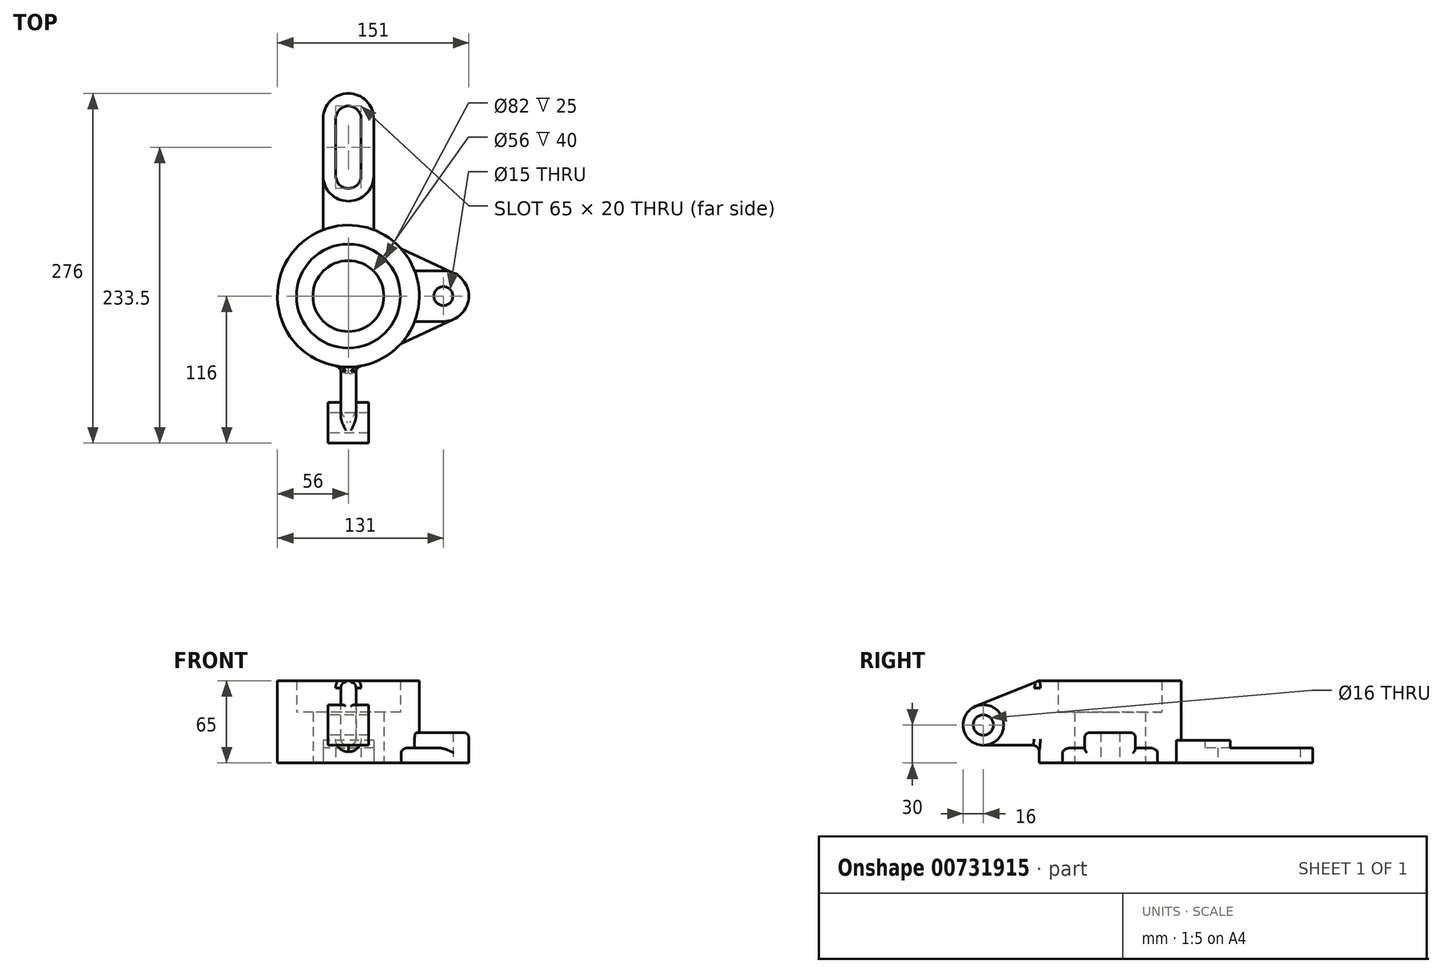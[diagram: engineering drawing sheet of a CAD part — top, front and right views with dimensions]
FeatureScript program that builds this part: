
annotation { "Feature Type Name" : "Feature", "Feature Type Description" : "" }
export const myFeature = defineFeature(function(context is Context, id is Id, definition is map)
    precondition{}
    {
        {
            var Q0;
            Q0=qCreatedBy(makeId("Top.planeOp"),FACE);
            var sketch = newSketch(context, id + "F0", { "sketchPlane" : qUnion([Q0])});
            skCircle(sketch, "E0", {"center": v(0, 0) * mm, "radius": 28 * mm});
            skCircle(sketch, "E1", {"center": v(0, 0) * mm, "radius": 41 * mm});
            skCircle(sketch, "E2", {"center": v(0, 0) * mm, "radius": 56 * mm});
            skSolve(sketch);
        }
        {
            var Q0;
            Q0=makeQuery(id+"F0.imprint","IMPRINT",FACE,{"disambiguationData":[TD([[makeQuery(id+"F0.imprint","IMPRINT",EDGE,{"derivedFrom":sQuery(id+"F0.wireOp",EDGE,"E1")}),-1.0]])]});
            extrude(context, id + "F1", {"entities" : qUnion([Q0]), "depth" : 65 * mm, "offsetDistance" : 25 * mm});
        }
        {
            var Q0;
            Q0=makeQuery(id+"F0.imprint","IMPRINT",FACE,{"disambiguationData":[TD([[makeQuery(id+"F0.imprint","IMPRINT",EDGE,{"derivedFrom":sQuery(id+"F0.wireOp",EDGE,"E0")}),-1.0]])]});
            extrude(context, id + "F2", {"entities" : qUnion([Q0]), "operationType" : NewBodyOperationType.ADD, "depth" : (65 - 25) * mm, "offsetDistance" : 25 * mm});
        }
        {
            var Q0;
            Q0=qCreatedBy(makeId("Top.planeOp"),FACE);
            var sketch = newSketch(context, id + "F3", { "sketchPlane" : qUnion([Q0])});
            skLineSegment(sketch, "E3", {"start": v(0, 95) * mm, "end": v(0, 140) * mm, "construction": true});
            skArc(sketch, "E4.0.startCap", {"start": v(20, 95) * mm, "mid": v(0, 75) * mm, "end": v(-20, 95) * mm});
            skArc(sketch, "E4.0.endCap", {"start": v(-20, 140) * mm, "mid": v(0, 160) * mm, "end": v(20, 140) * mm});
            skLineSegment(sketch, "E4.0.left", {"start": v(-20, 95) * mm, "end": v(-20, 140) * mm});
            skLineSegment(sketch, "E4.0.right", {"start": v(20, 95) * mm, "end": v(20, 140) * mm});
            skArc(sketch, "E5.0.startCap", {"start": v(10, 95) * mm, "mid": v(0, 85) * mm, "end": v(-10, 95) * mm});
            skArc(sketch, "E5.0.endCap", {"start": v(-10, 140) * mm, "mid": v(0, 150) * mm, "end": v(10, 140) * mm});
            skLineSegment(sketch, "E5.0.left", {"start": v(-10, 95) * mm, "end": v(-10, 140) * mm});
            skLineSegment(sketch, "E5.0.right", {"start": v(10, 95) * mm, "end": v(10, 140) * mm});
            skCircle(sketch, "E6.0", {"center": v(0, 0) * mm, "radius": 56 * mm});
            skLineSegment(sketch, "E7", {"start": v(-20, 95) * mm, "end": v(-20, 52.3) * mm});
            skLineSegment(sketch, "E8", {"start": v(20, 95) * mm, "end": v(20, 52.3) * mm});
            skSolve(sketch);
        }
        {
            var Q0;
            Q0=makeQuery(id+"F3.imprint","IMPRINT",FACE,{"disambiguationData":[TD([[makeQuery(id+"F3.imprint","IMPRINT",EDGE,{"derivedFrom":sQuery(id+"F3.wireOp",EDGE,"E4.0.startCap")}),1.0]])]});
            extrude(context, id + "F4", {"entities" : qUnion([Q0]), "operationType" : NewBodyOperationType.ADD, "depth" : 12 * mm, "offsetDistance" : 25 * mm});
        }
        {
            var Q0;
            Q0=makeQuery(id+"F3.imprint","IMPRINT",FACE,{"disambiguationData":[TD([[makeQuery(id+"F3.imprint","IMPRINT",EDGE,{"derivedFrom":sQuery(id+"F3.wireOp",EDGE,"E4.0.startCap")}),-1.0]])]});
            extrude(context, id + "F5", {"entities" : qUnion([Q0]), "operationType" : NewBodyOperationType.ADD, "depth" : 18 * mm, "offsetDistance" : 25 * mm});
        }
        {
            var Q0;
            Q0=qCreatedBy(makeId("Right.planeOp"),FACE);
            var sketch = newSketch(context, id + "F6", { "sketchPlane" : qUnion([Q0])});
            skCircle(sketch, "E9", {"center": v(-100, 30) * mm, "radius": 16 * mm});
            skCircle(sketch, "E10", {"center": v(-100, 30) * mm, "radius": 8 * mm});
            skLineSegment(sketch, "E11.0", {"start": v(-56, 65) * mm, "end": v(56, 65) * mm});
            skLineSegment(sketch, "E12", {"start": v(-56, 0) * mm, "end": v(-56, 65) * mm});
            skLineSegment(sketch, "E13", {"start": v(-56, 65) * mm, "end": v(-105.99, 44.84) * mm});
            skLineSegment(sketch, "E14", {"start": v(-100, 14) * mm, "end": v(-56, 14) * mm});
            skLineSegment(sketch, "E15", {"start": v(-56, 14) * mm, "end": v(-51, 14) * mm});
            skLineSegment(sketch, "E16", {"start": v(-51, 14) * mm, "end": v(-51, 65) * mm});
            skSolve(sketch);
        }
        {
            var Q0;
            {var subQ0=sQuery(id+"F6.wireOp",EDGE,"E13");Q0=makeQuery(id+"F6.imprint","IMPRINT",FACE,{"disambiguationData":[TD([[makeQuery(id+"F6.imprint","IMPRINT",EDGE,{"derivedFrom":subQ0}),1.0]])]});}
            var Q1;
            {var subQ4=sQuery(id+"F6.wireOp",EDGE,"E15");Q1=makeQuery(id+"F6.imprint","IMPRINT",FACE,{"disambiguationData":[TD([[makeQuery(id+"F6.imprint","IMPRINT",EDGE,{"derivedFrom":subQ4}),1.0]])]});}
            extrude(context, id + "F7", {"entities" : qUnion([Q0, Q1]), "operationType" : NewBodyOperationType.ADD, "depth" : 12 * mm, "offsetDistance" : 25 * mm, "symmetric" : true});
        }
        {
            var Q0;
            Q0=makeQuery(id+"F6.imprint","IMPRINT",FACE,{"disambiguationData":[TD([[makeQuery(id+"F6.imprint","IMPRINT",EDGE,{"derivedFrom":sQuery(id+"F6.wireOp",EDGE,"E10")}),-1.0]])]});
            extrude(context, id + "F8", {"entities" : qUnion([Q0]), "operationType" : NewBodyOperationType.ADD, "depth" : 32 * mm, "offsetDistance" : 25 * mm, "symmetric" : true});
        }
        {
            var Q0;
            Q0=qCreatedBy(makeId("Top.planeOp"),FACE);
            var sketch = newSketch(context, id + "F9", { "sketchPlane" : qUnion([Q0])});
            skArc(sketch, "E17", {"start": v(75, -20) * mm, "mid": v(95, 0) * mm, "end": v(75, 20) * mm});
            skCircle(sketch, "E18", {"center": v(75, 0) * mm, "radius": 7.5 * mm});
            skArc(sketch, "E19.0", {"start": v(-20, 52.3) * mm, "mid": v(0, -56) * mm, "end": v(20, 52.3) * mm});
            skLineSegment(sketch, "E20", {"start": v(75, -20) * mm, "end": v(52.3, -20) * mm});
            skLineSegment(sketch, "E21", {"start": v(0, 0) * mm, "end": v(75, 0) * mm, "construction": true});
            skLineSegment(sketch, "E22", {"start": v(83.4, -18.15) * mm, "end": v(41.6, -37.5) * mm});
            skLineSegment(sketch, "E23.MirrorCS", {"start": v(75, 20) * mm, "end": v(52.3, 20) * mm});
            skLineSegment(sketch, "E24.MirrorCS", {"start": v(83.4, 18.15) * mm, "end": v(41.6, 37.5) * mm});
            skSolve(sketch);
        }
        {
            var Q0;
            {var subQ0=sQuery(id+"F9.wireOp",EDGE,"E23.MirrorCS");Q0=makeQuery(id+"F9.imprint","IMPRINT",FACE,{"disambiguationData":[TD([[makeQuery(id+"F9.imprint","IMPRINT",EDGE,{"derivedFrom":subQ0}),-1.0]])]});}
            var Q1;
            {var subQ0=sQuery(id+"F9.wireOp",EDGE,"E20");Q1=makeQuery(id+"F9.imprint","IMPRINT",FACE,{"disambiguationData":[TD([[makeQuery(id+"F9.imprint","IMPRINT",EDGE,{"derivedFrom":subQ0}),1.0]])]});}
            extrude(context, id + "F10", {"entities" : qUnion([Q0, Q1]), "operationType" : NewBodyOperationType.ADD, "depth" : 12 * mm, "offsetDistance" : 25 * mm});
        }
        {
            var Q0;
            Q0=makeQuery(id+"F9.imprint","IMPRINT",FACE,{"disambiguationData":[TD([[makeQuery(id+"F9.imprint","IMPRINT",EDGE,{"derivedFrom":sQuery(id+"F9.wireOp",EDGE,"E18")}),-1.0]])]});
            extrude(context, id + "F11", {"entities" : qUnion([Q0]), "operationType" : NewBodyOperationType.ADD, "depth" : 24 * mm, "offsetDistance" : 25 * mm});
        }
        {
            var Q0;
            Q0=makeQuery(id+"F4.opExtrude","CAP_EDGE",EDGE,{"disambiguationData":[OSD([sQuery(id+"F3.wireOp",EDGE,"E4.0.startCap")])],"isStart":false});
            var Q1;
            Q1=makeQuery(id+"F4.opExtrude","CAP_EDGE",EDGE,{"disambiguationData":[OSD([sQuery(id+"F3.wireOp",EDGE,"E8")])],"isStart":false});
            var Q2;
            Q2=makeQuery(id+"F4.opExtrude","CAP_EDGE",EDGE,{"disambiguationData":[OSD([sQuery(id+"F3.wireOp",EDGE,"E7")])],"isStart":false});
            var Q3;
            Q3=makeQuery(id+"F4.opExtrude","CAP_EDGE",EDGE,{"disambiguationData":[OSD([sQuery(id+"F3.wireOp",EDGE,"E6.0")])],"isStart":false});
            var Q4;
            Q4=makeQuery(id+"F7.opExtrude","CAP_EDGE",EDGE,{"disambiguationData":[OSD([sQuery(id+"F6.wireOp",EDGE,"E9")])],"isStart":false});
            var Q5;
            Q5=makeQuery(id+"F7.opExtrude","CAP_EDGE",EDGE,{"disambiguationData":[OSD([sQuery(id+"F6.wireOp",EDGE,"E9")])],"isStart":true});
            var Q6;
            Q6=makeQuery(id+"F7.opExtrude","CAP_EDGE",EDGE,{"disambiguationData":[OSD([sQuery(id+"F6.wireOp",EDGE,"E13")])],"isStart":false});
            var Q7;
            Q7=makeQuery(id+"F7.opExtrude","CAP_EDGE",EDGE,{"disambiguationData":[OSD([sQuery(id+"F6.wireOp",EDGE,"E13")])],"isStart":true});
            var Q8;
            Q8=makeQuery(id+"F11.opExtrude","SWEPT_EDGE",EDGE,{"disambiguationData":[OSD([sQuery(id+"F9.wireOp",EDGE,"E19.0"),sQuery(id+"F9.wireOp",EDGE,"E20")])]});
            var Q9;
            Q9=makeQuery(id+"F11.opExtrude","SWEPT_EDGE",EDGE,{"disambiguationData":[OSD([sQuery(id+"F9.wireOp",EDGE,"E19.0"),sQuery(id+"F9.wireOp",EDGE,"E23.MirrorCS")])]});
            var Q10;
            Q10=makeQuery(id+"F11.opExtrude","CAP_EDGE",EDGE,{"disambiguationData":[OSD([sQuery(id+"F9.wireOp",EDGE,"E19.0")])],"isStart":false});
            var Q11;
            Q11=makeQuery(id+"F11.opExtrude","CAP_EDGE",EDGE,{"disambiguationData":[OSD([sQuery(id+"F9.wireOp",EDGE,"E20")])],"isStart":false});
            var Q12;
            Q12=makeQuery(id+"F10.opExtrude","CAP_EDGE",EDGE,{"disambiguationData":[OSD([sQuery(id+"F9.wireOp",EDGE,"E20")])],"isStart":false});
            var Q13;
            {var subQ0=sQuery(id+"F9.wireOp",EDGE,"E19.0");Q13=makeQuery(id+"F10.opExtrude","CAP_EDGE",EDGE,{"disambiguationData":[OSD([subQ0]),TDD([makeQuery(id+"F9.imprint","IMPRINT",EDGE,{"disambiguationData":[TD([[makeQuery(id+"F9.imprint","INTERSECT",VERTEX,{"derivedFrom":[subQ0,sQuery(id+"F9.wireOp",EDGE,"E20")]}),1.0]])],"derivedFrom":subQ0})])],"isStart":false});}
            var Q14;
            Q14=makeQuery(id+"F10.opExtrude","CAP_EDGE",EDGE,{"disambiguationData":[OSD([sQuery(id+"F9.wireOp",EDGE,"E22")])],"isStart":false});
            var Q15;
            Q15=makeQuery(id+"F10.opExtrude","CAP_EDGE",EDGE,{"disambiguationData":[OSD([sQuery(id+"F9.wireOp",EDGE,"E23.MirrorCS")])],"isStart":false});
            var Q16;
            {var subQ0=sQuery(id+"F9.wireOp",EDGE,"E19.0");Q16=makeQuery(id+"F10.opExtrude","CAP_EDGE",EDGE,{"disambiguationData":[OSD([subQ0]),TDD([makeQuery(id+"F9.imprint","IMPRINT",EDGE,{"disambiguationData":[TD([[makeQuery(id+"F9.imprint","INTERSECT",VERTEX,{"derivedFrom":[subQ0,sQuery(id+"F9.wireOp",EDGE,"E23.MirrorCS")]}),-1.0]])],"derivedFrom":subQ0})])],"isStart":false});}
            var Q17;
            Q17=makeQuery(id+"F10.opExtrude","CAP_EDGE",EDGE,{"disambiguationData":[OSD([sQuery(id+"F9.wireOp",EDGE,"E24.MirrorCS")])],"isStart":false});
            fillet(context, id + "F12", {"entities" : qUnion([Q0, Q1, Q2, Q3, Q4, Q5, Q6, Q7, Q8, Q9, Q10, Q11, Q12, Q13, Q14, Q15, Q16, Q17]), "radius" : 4 * mm, "tangentPropagation" : true, "allowEdgeOverflow" : false});
        }
        {
            var Q0;
            Q0=makeQuery(id+"F7.boolean.opBoolean","INTERSECT",EDGE,{"derivedFrom":[makeQuery(id+"F1.opExtrude","SWEPT_FACE",FACE,{"disambiguationData":[OSD([sQuery(id+"F0.wireOp",EDGE,"E2")])]}),makeQuery(id+"F7.opExtrude","CAP_FACE",FACE,{"disambiguationData":[OSD([sQuery(id+"F6.wireOp",EDGE,"E9"),sQuery(id+"F6.wireOp",EDGE,"E11.0"),sQuery(id+"F6.wireOp",EDGE,"E13"),sQuery(id+"F6.wireOp",EDGE,"E14"),sQuery(id+"F6.wireOp",EDGE,"E15"),sQuery(id+"F6.wireOp",EDGE,"E16")])],"isStart":false})]});
            var Q1;
            Q1=makeQuery(id+"F7.boolean.opBoolean","INTERSECT",EDGE,{"derivedFrom":[makeQuery(id+"F1.opExtrude","SWEPT_FACE",FACE,{"disambiguationData":[OSD([sQuery(id+"F0.wireOp",EDGE,"E2")])]}),makeQuery(id+"F7.opExtrude","CAP_FACE",FACE,{"disambiguationData":[OSD([sQuery(id+"F6.wireOp",EDGE,"E9"),sQuery(id+"F6.wireOp",EDGE,"E11.0"),sQuery(id+"F6.wireOp",EDGE,"E13"),sQuery(id+"F6.wireOp",EDGE,"E14"),sQuery(id+"F6.wireOp",EDGE,"E15"),sQuery(id+"F6.wireOp",EDGE,"E16")])],"isStart":true})]});
            var Q2;
            Q2=makeQuery(id+"F7.opExtrude","CAP_EDGE",EDGE,{"disambiguationData":[OSD([sQuery(id+"F6.wireOp",EDGE,"E14"),sQuery(id+"F6.wireOp",EDGE,"E15")])],"isStart":true});
            var Q3;
            Q3=makeQuery(id+"F7.opExtrude","CAP_EDGE",EDGE,{"disambiguationData":[OSD([sQuery(id+"F6.wireOp",EDGE,"E14"),sQuery(id+"F6.wireOp",EDGE,"E15")])],"isStart":false});
            fillet(context, id + "F13", {"entities" : qUnion([Q0, Q1, Q2, Q3]), "radius" : 5 * mm, "tangentPropagation" : true, "allowEdgeOverflow" : false});
        }
    });
